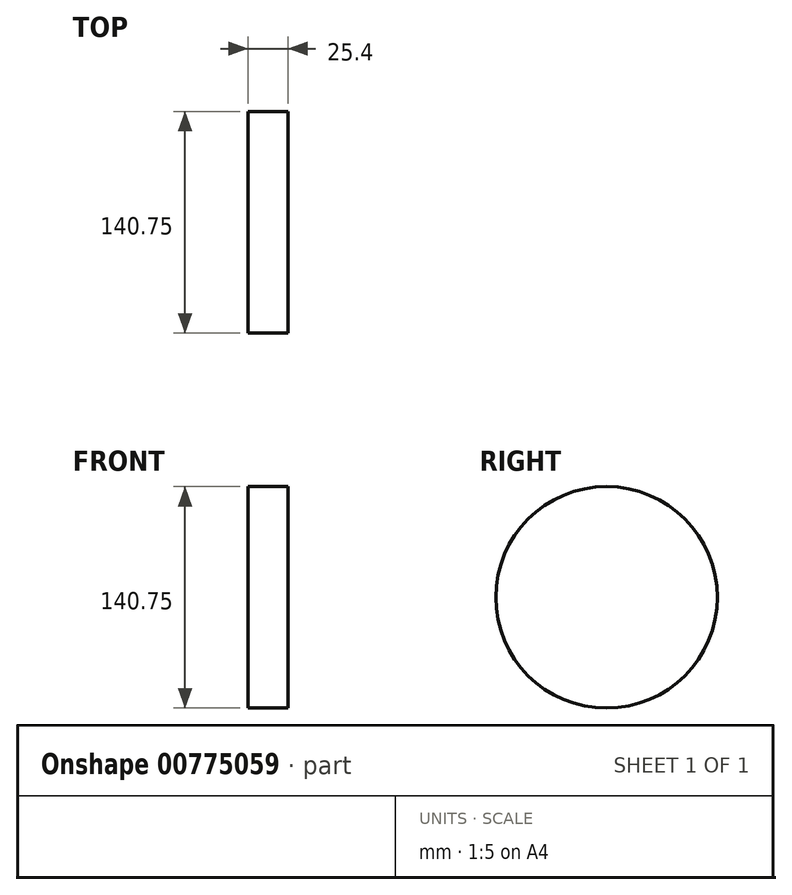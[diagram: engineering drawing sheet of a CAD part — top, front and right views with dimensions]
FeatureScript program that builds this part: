
annotation { "Feature Type Name" : "Feature", "Feature Type Description" : "" }
export const myFeature = defineFeature(function(context is Context, id is Id, definition is map)
    precondition{}
    {
        {
            var Q0;
            Q0=qCreatedBy(makeId("Right.planeOp"),FACE);
            var sketch = newSketch(context, id + "F0", { "sketchPlane" : qUnion([Q0])});
            skCircle(sketch, "E0", {"center": v(66.65, 22.6) * mm, "radius": 70.37 * mm});
            skPoint(sketch, "E0.first.point", {"position": v(0, 0) * mm});
            skPoint(sketch, "E0.second.point", {"position": v(74.85, -47.3) * mm});
            skPoint(sketch, "E0.third.point", {"position": v(0, 45.19) * mm});
            skCircle(sketch, "E1", {"center": v(-77.08, 133.35) * mm, "radius": 17.22 * mm});
            skPoint(sketch, "E1.first.point", {"position": v(-61.96, 125.1) * mm});
            skPoint(sketch, "E1.second.point", {"position": v(-94.22, 131.7) * mm});
            skPoint(sketch, "E1.third.point", {"position": v(-62.7, 142.82) * mm});
            skSolve(sketch);
        }
        {
            var Q0;
            Q0=sQuery(id+"F0.wireOp",EDGE,"E0");
            extrude(context, id + "F1", {"bodyType" : ToolBodyType.SURFACE, "surfaceEntities" : qUnion([Q0]), "depth" : 25.4 * mm, "offsetDistance" : 25.4 * mm});
        }
    });
